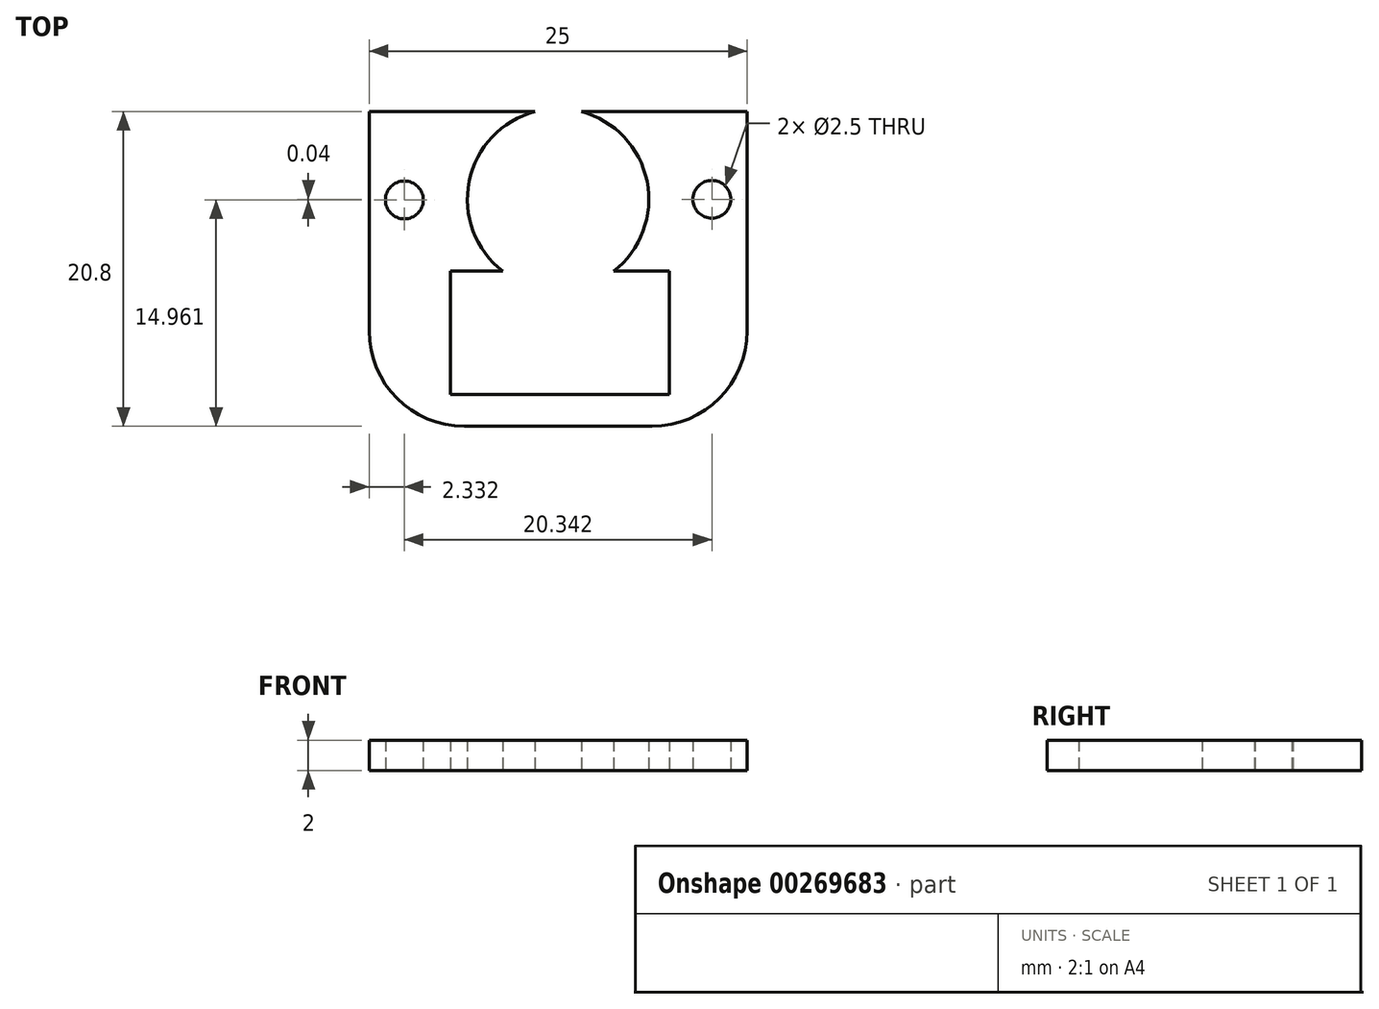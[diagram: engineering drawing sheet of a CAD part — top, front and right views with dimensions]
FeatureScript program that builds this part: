
annotation { "Feature Type Name" : "Feature", "Feature Type Description" : "" }
export const myFeature = defineFeature(function(context is Context, id is Id, definition is map)
    precondition{}
    {
        {
            var Q0;
            Q0=qCreatedBy(makeId("Top.planeOp"),FACE);
            var sketch = newSketch(context, id + "F0", { "sketchPlane" : qUnion([Q0])});
            skCircle(sketch, "E0", {"center": v(1.21, -12) * mm, "radius": 6 * mm});
            skLineSegment(sketch, "E1.bottom", {"start": v(5.96, -16.76) * mm, "end": v(-3.54, -16.76) * mm});
            skPoint(sketch, "E2.oppositeSnap0", {"position": v(10.18, -24.92) * mm});
            skLineSegment(sketch, "E2.bottom", {"start": v(-5.92, -16.76) * mm, "end": v(8.58, -16.76) * mm});
            skLineSegment(sketch, "E2.top", {"start": v(-5.92, -24.92) * mm, "end": v(8.58, -24.92) * mm});
            skLineSegment(sketch, "E2.left", {"start": v(-5.92, -16.76) * mm, "end": v(-5.92, -24.92) * mm});
            skLineSegment(sketch, "E2.right", {"start": v(8.58, -16.76) * mm, "end": v(8.58, -24.92) * mm});
            skLineSegment(sketch, "E3", {"start": v(-11.29, -21.3) * mm, "end": v(-11.29, -27) * mm});
            skLineSegment(sketch, "E4", {"start": v(-11.29, -6.2) * mm, "end": v(13.71, -6.2) * mm});
            skCircle(sketch, "E5", {"center": v(1.21, -12) * mm, "radius": 3.8 * mm});
            skPoint(sketch, "E6.endSnap0", {"position": v(-11.29, -24.16) * mm});
            skLineSegment(sketch, "E7", {"start": v(-11.29, -27) * mm, "end": v(-11.29, -29) * mm});
            skCircle(sketch, "E8", {"center": v(11.38, -12) * mm, "radius": 1.25 * mm});
            skCircle(sketch, "E9.MirrorC", {"center": v(-8.96, -12.05) * mm, "radius": 1.25 * mm});
            skLineSegment(sketch, "E10", {"start": v(13.71, -22.12) * mm, "end": v(13.71, -29.82) * mm});
            skLineSegment(sketch, "E11", {"start": v(-11.29, -27) * mm, "end": v(13.71, -27) * mm});
            skLineSegment(sketch, "E12", {"start": v(-11.29, -6.2) * mm, "end": v(-11.29, -21.3) * mm});
            skLineSegment(sketch, "E13", {"start": v(13.71, -6.2) * mm, "end": v(13.71, -22.12) * mm});
            skSolve(sketch);
        }
        {
            var Q0;
            Q0=makeQuery(id+"F0.imprint","IMPRINT",FACE,{"disambiguationData":[TD([[makeQuery(id+"F0.imprint","IMPRINT",EDGE,{"derivedFrom":sQuery(id+"F0.wireOp",EDGE,"E2.top")}),-1.0]])]});
            extrude(context, id + "F1", {"entities" : qUnion([Q0]), "depth" : 2 * mm});
        }
        {
            var Q0;
            Q0=makeQuery(id+"F1.opExtrude","SWEPT_EDGE",EDGE,{"disambiguationData":[OSD([sQuery(id+"F0.wireOp",EDGE,"E3"),sQuery(id+"F0.wireOp",EDGE,"E11")])]});
            var Q1;
            Q1=makeQuery(id+"F1.opExtrude","SWEPT_EDGE",EDGE,{"disambiguationData":[OSD([sQuery(id+"F0.wireOp",EDGE,"E10"),sQuery(id+"F0.wireOp",EDGE,"E11")])]});
            fillet(context, id + "F2", {"entities" : qUnion([Q0, Q1]), "radius" : 6.3 * mm, "tangentPropagation" : true, "allowEdgeOverflow" : false});
        }
    });
